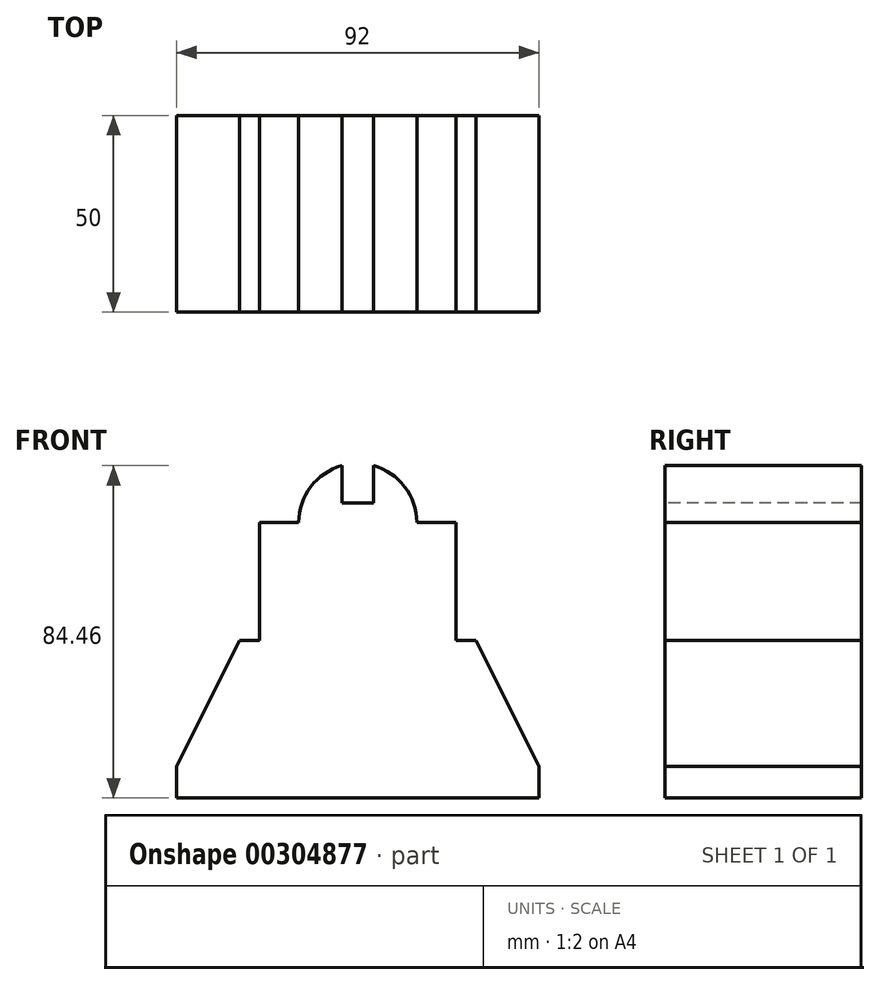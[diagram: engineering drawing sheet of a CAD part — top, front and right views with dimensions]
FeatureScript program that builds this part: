
annotation { "Feature Type Name" : "Feature", "Feature Type Description" : "" }
export const myFeature = defineFeature(function(context is Context, id is Id, definition is map)
    precondition{}
    {
        {
            var Q0;
            Q0=qCreatedBy(makeId("Top.planeOp"),FACE);
            var sketch = newSketch(context, id + "F0", { "sketchPlane" : qUnion([Q0])});
            skLineSegment(sketch, "E0.bottom", {"start": v(46, -25) * mm, "end": v(-46, -25) * mm});
            skLineSegment(sketch, "E0.top", {"start": v(46, 25) * mm, "end": v(-46, 25) * mm});
            skLineSegment(sketch, "E0.left", {"start": v(46, -25) * mm, "end": v(46, 25) * mm});
            skLineSegment(sketch, "E0.right", {"start": v(-46, -25) * mm, "end": v(-46, 25) * mm});
            skPoint(sketch, "E0.middle", {"position": v(0, 0) * mm});
            skSolve(sketch);
        }
        {
            var Q0;
            Q0=makeQuery(id+"F0.imprint","IMPRINT",FACE,{"disambiguationData":[TD([[makeQuery(id+"F0.imprint","IMPRINT",EDGE,{"derivedFrom":sQuery(id+"F0.wireOp",EDGE,"E0.bottom")}),-1.0]])]});
            extrude(context, id + "F1", {"entities" : qUnion([Q0]), "depth" : 40 * mm});
        }
        {
            var Q0;
            Q0=makeQuery(id+"F1.opExtrude","CAP_EDGE",EDGE,{"disambiguationData":[OSD([sQuery(id+"F0.wireOp",EDGE,"E0.left")])],"isStart":false});
            chamfer(context, id + "F2", {"entities" : qUnion([Q0]), "chamferType" : ChamferType.TWO_OFFSETS, "width1" : 16 * mm, "oppositeDirection" : false, "width2" : 32 * mm, "tangentPropagation" : true});
        }
        {
            var Q0;
            Q0=makeQuery(id+"F1.opExtrude","CAP_EDGE",EDGE,{"disambiguationData":[OSD([sQuery(id+"F0.wireOp",EDGE,"E0.right")])],"isStart":false});
            chamfer(context, id + "F3", {"entities" : qUnion([Q0]), "chamferType" : ChamferType.TWO_OFFSETS, "width1" : 16 * mm, "oppositeDirection" : true, "width2" : 32 * mm, "tangentPropagation" : true});
        }
        {
            var Q0;
            Q0=makeQuery(id+"F1.opExtrude","CAP_FACE",FACE,{"disambiguationData":[OSD([sQuery(id+"F0.wireOp",EDGE,"E0.bottom"),sQuery(id+"F0.wireOp",EDGE,"E0.top"),sQuery(id+"F0.wireOp",EDGE,"E0.left"),sQuery(id+"F0.wireOp",EDGE,"E0.right")])],"isStart":false});
            var sketch = newSketch(context, id + "F4", { "sketchPlane" : qUnion([Q0])});
            skSolve(sketch);
        }
        {
            var Q0;
            {var subQ3=sQuery(id+"F0.wireOp",EDGE,"E0.bottom");Q0=makeQuery(id+"F4.imprint","IMPRINT",FACE,{"disambiguationData":[TD([[makeQuery(id+"F4.imprint","IMPRINT",EDGE,{"derivedFrom":makeQuery(id+"F1.opExtrude","CAP_EDGE",EDGE,{"disambiguationData":[OSD([subQ3])],"isStart":false})}),-1.0]])]});}
            var sketch = newSketch(context, id + "F5", { "sketchPlane" : qUnion([Q0])});
            skLineSegment(sketch, "E1.bottom", {"start": v(25, -25) * mm, "end": v(-25, -25) * mm});
            skLineSegment(sketch, "E1.top", {"start": v(25, 25) * mm, "end": v(-25, 25) * mm});
            skLineSegment(sketch, "E1.left", {"start": v(25, -25) * mm, "end": v(25, 25) * mm});
            skLineSegment(sketch, "E1.right", {"start": v(-25, -25) * mm, "end": v(-25, 25) * mm});
            skPoint(sketch, "E1.middle", {"position": v(0, 0) * mm});
            skSolve(sketch);
        }
        {
            var Q0;
            Q0 = qSketchRegion(id + "F5", true);
            extrude(context, id + "F6", {"entities" : qUnion([Q0]), "operationType" : NewBodyOperationType.ADD, "depth" : 30 * mm});
        }
        {
            var Q0;
            Q0=makeQuery(id+"F6.boolean.opBoolean","MERGE",FACE,{"derivedFrom":[makeQuery(id+"F1.opExtrude","SWEPT_FACE",FACE,{"disambiguationData":[OSD([sQuery(id+"F0.wireOp",EDGE,"E0.bottom")])]}),makeQuery(id+"F6.opExtrude","SWEPT_FACE",FACE,{"disambiguationData":[OSD([sQuery(id+"F5.wireOp",EDGE,"E1.bottom")])]})]});
            var sketch = newSketch(context, id + "F7", { "sketchPlane" : qUnion([Q0])});
            skCircle(sketch, "E2", {"center": v(0, 70) * mm, "radius": 15 * mm});
            skSolve(sketch);
        }
        {
            var Q0;
            {var subQ0=sQuery(id+"F7.wireOp",EDGE,"E2");var subQ1=makeQuery(id+"F6.opExtrude","CAP_EDGE",EDGE,{"disambiguationData":[OSD([sQuery(id+"F5.wireOp",EDGE,"E1.bottom")])],"isStart":false});var subQ2=makeQuery(id+"F7.imprint","INTERSECT",VERTEX,{"disambiguationData":[OD(0.0)],"derivedFrom":[subQ1,subQ0]});Q0=makeQuery(id+"F7.imprint","IMPRINT",FACE,{"disambiguationData":[TD([[makeQuery(id+"F7.imprint","IMPRINT",EDGE,{"disambiguationData":[TD([[subQ2,-1.0]])],"derivedFrom":subQ0}),1.0]])]});}
            extrude(context, id + "F8", {"entities" : qUnion([Q0]), "operationType" : NewBodyOperationType.ADD, "oppositeDirection" : true, "depth" : 50 * mm});
        }
        {
            var Q0;
            {var subQ0=sQuery(id+"F5.wireOp",EDGE,"E1.bottom");Q0=makeQuery(id+"F8.boolean.opBoolean","MERGE",FACE,{"derivedFrom":[makeQuery(id+"F6.boolean.opBoolean","MERGE",FACE,{"derivedFrom":[makeQuery(id+"F1.opExtrude","SWEPT_FACE",FACE,{"disambiguationData":[OSD([sQuery(id+"F0.wireOp",EDGE,"E0.bottom")])]}),makeQuery(id+"F6.opExtrude","SWEPT_FACE",FACE,{"disambiguationData":[OSD([subQ0])]})]}),makeQuery(id+"F8.opExtrude","CAP_FACE",FACE,{"disambiguationData":[OSD([subQ0,sQuery(id+"F7.wireOp",EDGE,"E2")])],"isStart":true})]});}
            var sketch = newSketch(context, id + "F9", { "sketchPlane" : qUnion([Q0])});
            skLineSegment(sketch, "E3.bottom", {"start": v(4, 75) * mm, "end": v(-4, 75) * mm});
            skLineSegment(sketch, "E3.top", {"start": v(4, 95) * mm, "end": v(-4, 95) * mm});
            skLineSegment(sketch, "E3.left", {"start": v(4, 75) * mm, "end": v(4, 95) * mm});
            skLineSegment(sketch, "E3.right", {"start": v(-4, 75) * mm, "end": v(-4, 95) * mm});
            skPoint(sketch, "E3.middle", {"position": v(0, 85) * mm});
            skSolve(sketch);
        }
        {
            var Q0;
            Q0 = qSketchRegion(id + "F9", true);
            extrude(context, id + "F10", {"entities" : qUnion([Q0]), "operationType" : NewBodyOperationType.REMOVE, "endBound" : BoundingType.THROUGH_ALL, "oppositeDirection" : true, "depth" : 25 * mm});
        }
    });
